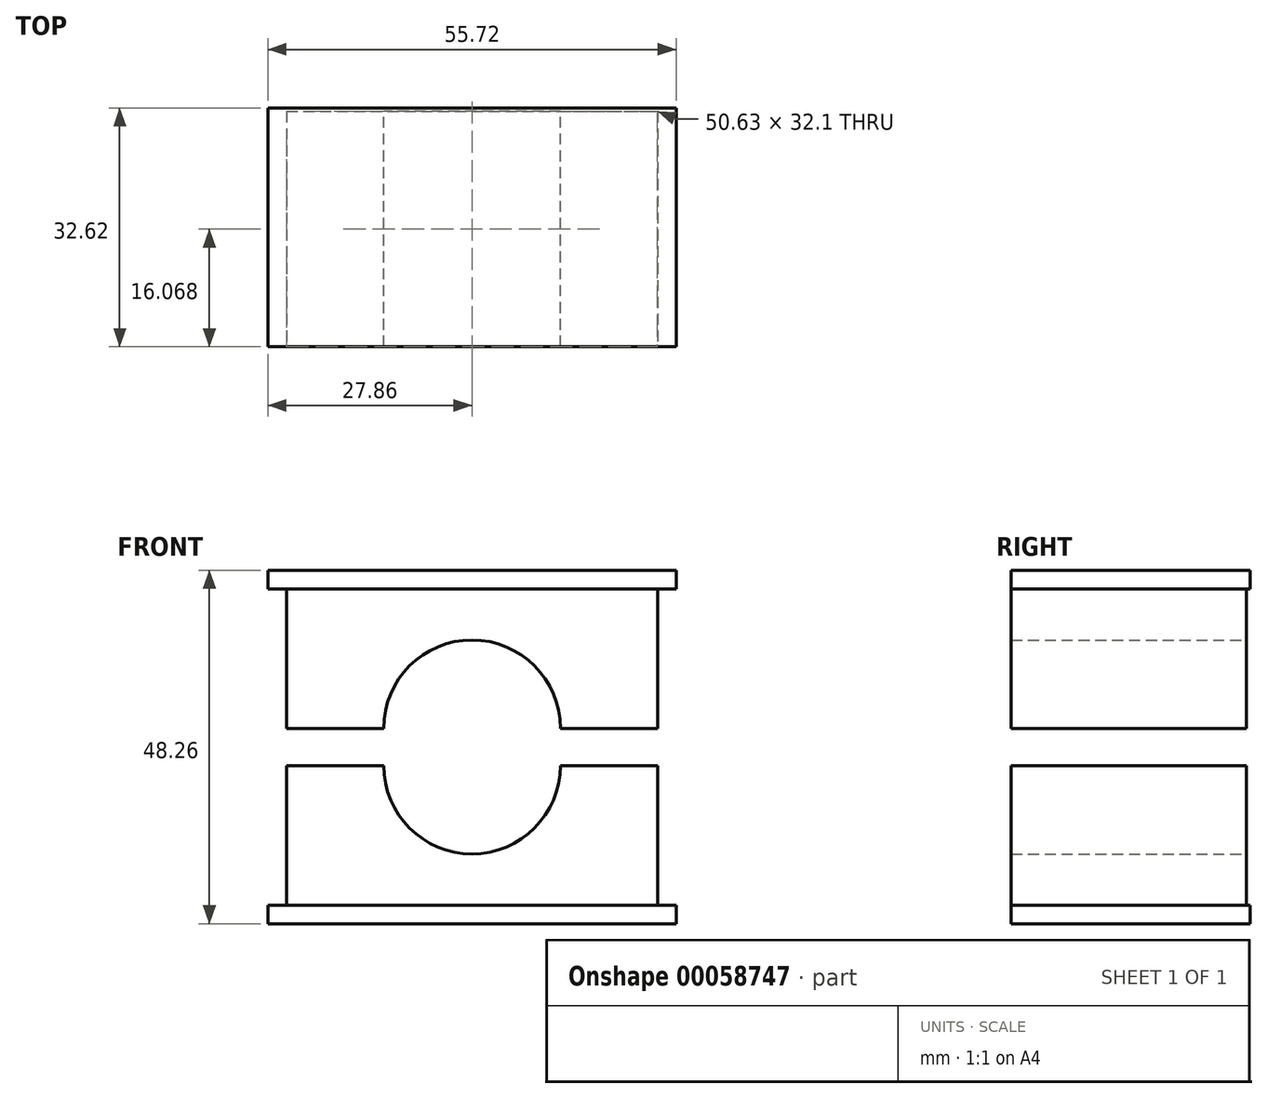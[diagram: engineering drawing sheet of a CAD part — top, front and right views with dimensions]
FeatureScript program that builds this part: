
annotation { "Feature Type Name" : "Feature", "Feature Type Description" : "" }
export const myFeature = defineFeature(function(context is Context, id is Id, definition is map)
    precondition{}
    {
        {
            var Q0;
            Q0=qCreatedBy(makeId("Top.planeOp"),FACE);
            var sketch = newSketch(context, id + "F0", { "sketchPlane" : qUnion([Q0])});
            skLineSegment(sketch, "E0.bottom", {"start": v(-41.36, 40.24) * mm, "end": v(34.68, 40.24) * mm});
            skLineSegment(sketch, "E0.top", {"start": v(-41.36, 0) * mm, "end": v(34.68, 0) * mm});
            skLineSegment(sketch, "E0.left", {"start": v(-41.36, 40.24) * mm, "end": v(-41.36, 0) * mm});
            skLineSegment(sketch, "E0.right", {"start": v(34.68, 40.24) * mm, "end": v(34.68, 0) * mm});
            skSolve(sketch);
        }
        {
            var Q0;
            Q0=makeQuery(id+"F0.imprint","IMPRINT",FACE,{"disambiguationData":[TD([[makeQuery(id+"F0.imprint","IMPRINT",EDGE,{"derivedFrom":sQuery(id+"F0.wireOp",EDGE,"E0.bottom")}),-1.0]])]});
            extrude(context, id + "F1", {"entities" : qUnion([Q0]), "depth" : 2.54 * mm});
        }
        {
            var Q0;
            Q0=makeQuery(id+"F1.opExtrude","CAP_FACE",FACE,{"disambiguationData":[OSD([sQuery(id+"F0.wireOp",EDGE,"E0.bottom"),sQuery(id+"F0.wireOp",EDGE,"E0.top"),sQuery(id+"F0.wireOp",EDGE,"E0.left"),sQuery(id+"F0.wireOp",EDGE,"E0.right")])],"isStart":false});
            var sketch = newSketch(context, id + "F2", { "sketchPlane" : qUnion([Q0])});
            skLineSegment(sketch, "E1.bottom", {"start": v(-28.66, 39.74) * mm, "end": v(21.98, 39.74) * mm});
            skLineSegment(sketch, "E1.top", {"start": v(-28.66, 0.02) * mm, "end": v(21.98, 0.02) * mm});
            skLineSegment(sketch, "E1.left", {"start": v(-28.66, 39.74) * mm, "end": v(-28.66, 0.02) * mm});
            skLineSegment(sketch, "E1.right", {"start": v(21.98, 39.74) * mm, "end": v(21.98, 0.02) * mm});
            skSolve(sketch);
        }
        {
            var Q0;
            Q0=makeQuery(id+"F2.imprint","IMPRINT",FACE,{"disambiguationData":[TD([[makeQuery(id+"F2.imprint","IMPRINT",EDGE,{"derivedFrom":sQuery(id+"F2.wireOp",EDGE,"E1.bottom")}),-1.0]])]});
            extrude(context, id + "F3", {"entities" : qUnion([Q0]), "operationType" : NewBodyOperationType.ADD, "depth" : 19.05 * mm});
        }
        {
            var Q0;
            Q0=makeQuery(id+"F3.opExtrude","SWEPT_FACE",FACE,{"disambiguationData":[OSD([sQuery(id+"F2.wireOp",EDGE,"E1.bottom")])]});
            var sketch = newSketch(context, id + "F4", { "sketchPlane" : qUnion([Q0])});
            skCircle(sketch, "E2", {"center": v(3.34, 21.59) * mm, "radius": 12.07 * mm});
            skSolve(sketch);
        }
        {
            var Q0;
            Q0 = qSketchRegion(id + "F4", true);
            extrude(context, id + "F5", {"entities" : qUnion([Q0]), "operationType" : NewBodyOperationType.REMOVE, "oppositeDirection" : true, "depth" : 50.8 * mm});
        }
        {
            var Q0;
            Q0=qCreatedBy(makeId("Top.planeOp"),FACE);
            cPlane(context, id + "F6", {"entities" : qUnion([Q0]), "cplaneType" : CPlaneType.OFFSET, "offset" : 24.13 * mm, "width" : 152.4 * mm, "height" : 152.4 * mm});
        }
        {
            var Q0;
            Q0=makeQuery(id+"F1.opExtrude","SWEPT_BODY",BODY,{"disambiguationData":[OSD([sQuery(id+"F0.wireOp",EDGE,"E0.bottom"),sQuery(id+"F0.wireOp",EDGE,"E0.top"),sQuery(id+"F0.wireOp",EDGE,"E0.left"),sQuery(id+"F0.wireOp",EDGE,"E0.right")])]});
            var Q1;
            Q1=qCreatedBy(id+"F6.planeOp",FACE);
            mirror(context, id + "F7", {"operationType" : NewBodyOperationType.ADD, "entities" : qUnion([Q0]), "mirrorPlane" : qUnion([Q1])});
        }
        {
            var Q0;
            Q0=makeQuery(id+"F1.opExtrude","SWEPT_FACE",FACE,{"disambiguationData":[OSD([sQuery(id+"F0.wireOp",EDGE,"E0.top")])]});
            var Q1;
            {var subQ0=makeQuery(id+"F3.opExtrude","SWEPT_FACE",FACE,{"disambiguationData":[OSD([sQuery(id+"F2.wireOp",EDGE,"E1.bottom")])]});Q1=makeQuery(id+"F7.boolean.opBoolean","MERGE",FACE,{"derivedFrom":[subQ0,makeQuery(id+"F7.opPattern","COPY",FACE,{"derivedFrom":subQ0,"instanceName":"1"})]});}
            extrude(context, id + "F8", {"entities" : qUnion([Q0, Q1]), "operationType" : NewBodyOperationType.REMOVE, "depth" : 38.1 * mm});
        }
        {
            var Q0;
            Q0=makeQuery(id+"F8.boolean.opBoolean","COPY",FACE,{"derivedFrom":makeQuery(id+"F8.opExtrude","CAP_FACE",FACE,{"disambiguationData":[OSD([sQuery(id+"F2.wireOp",EDGE,"E1.bottom")])],"isStart":false})});
            extrude(context, id + "F9", {"entities" : qUnion([Q0]), "operationType" : NewBodyOperationType.ADD, "depth" : 30.48 * mm});
        }
        {
            var Q0;
            Q0=makeQuery(id+"F7.opPattern","COPY",FACE,{"derivedFrom":makeQuery(id+"F1.opExtrude","SWEPT_FACE",FACE,{"disambiguationData":[OSD([sQuery(id+"F0.wireOp",EDGE,"E0.bottom")])]}),"instanceName":"1"});
            extrude(context, id + "F10", {"entities" : qUnion([Q0]), "operationType" : NewBodyOperationType.REMOVE, "oppositeDirection" : true, "depth" : 7.62 * mm});
        }
        {
            var Q0;
            Q0=makeQuery(id+"F1.opExtrude","SWEPT_FACE",FACE,{"disambiguationData":[OSD([sQuery(id+"F0.wireOp",EDGE,"E0.bottom")])]});
            extrude(context, id + "F11", {"entities" : qUnion([Q0]), "operationType" : NewBodyOperationType.REMOVE, "oppositeDirection" : true, "depth" : 7.62 * mm});
        }
        {
            var Q0;
            Q0=makeQuery(id+"F1.opExtrude","SWEPT_FACE",FACE,{"disambiguationData":[OSD([sQuery(id+"F0.wireOp",EDGE,"E0.left")])]});
            extrude(context, id + "F12", {"entities" : qUnion([Q0]), "operationType" : NewBodyOperationType.REMOVE, "oppositeDirection" : true, "depth" : 10.16 * mm});
        }
        {
            var Q0;
            Q0=makeQuery(id+"F1.opExtrude","SWEPT_FACE",FACE,{"disambiguationData":[OSD([sQuery(id+"F0.wireOp",EDGE,"E0.right")])]});
            extrude(context, id + "F13", {"entities" : qUnion([Q0]), "operationType" : NewBodyOperationType.REMOVE, "oppositeDirection" : true, "depth" : 10.16 * mm});
        }
        {
            var Q0;
            Q0=makeQuery(id+"F7.opPattern","COPY",FACE,{"derivedFrom":makeQuery(id+"F1.opExtrude","SWEPT_FACE",FACE,{"disambiguationData":[OSD([sQuery(id+"F0.wireOp",EDGE,"E0.right")])]}),"instanceName":"1"});
            extrude(context, id + "F14", {"entities" : qUnion([Q0]), "operationType" : NewBodyOperationType.REMOVE, "oppositeDirection" : true, "depth" : 10.16 * mm});
        }
        {
            var Q0;
            Q0=makeQuery(id+"F7.opPattern","COPY",FACE,{"derivedFrom":makeQuery(id+"F1.opExtrude","SWEPT_FACE",FACE,{"disambiguationData":[OSD([sQuery(id+"F0.wireOp",EDGE,"E0.left")])]}),"instanceName":"1"});
            extrude(context, id + "F15", {"entities" : qUnion([Q0]), "operationType" : NewBodyOperationType.REMOVE, "oppositeDirection" : true, "depth" : 10.16 * mm});
        }
    });
